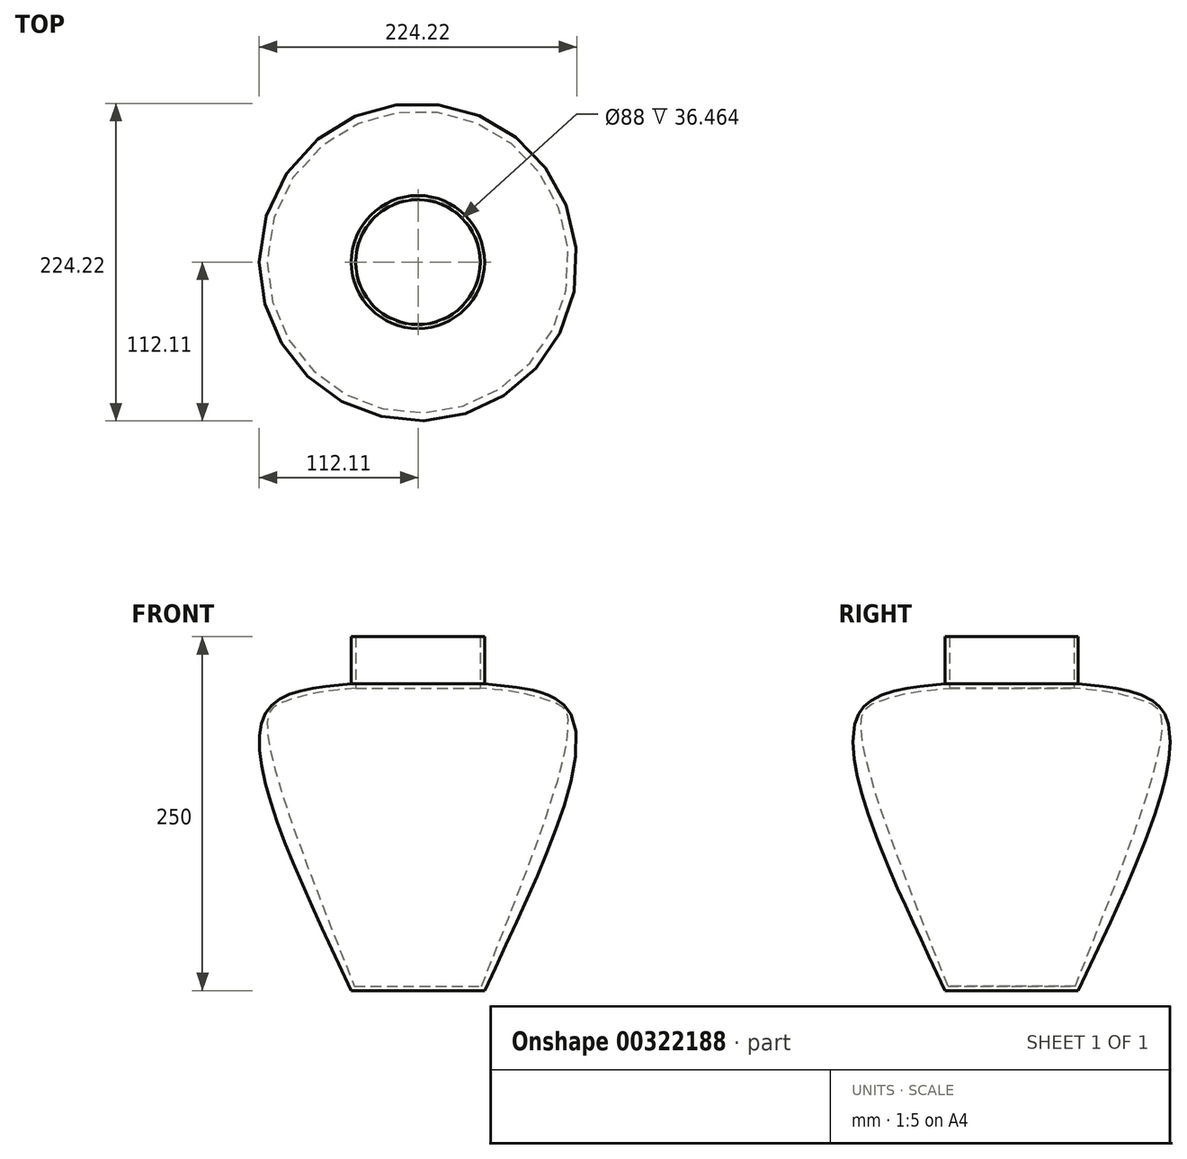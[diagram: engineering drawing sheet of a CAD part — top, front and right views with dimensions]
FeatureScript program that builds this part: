
annotation { "Feature Type Name" : "Feature", "Feature Type Description" : "" }
export const myFeature = defineFeature(function(context is Context, id is Id, definition is map)
    precondition{}
    {
        {
            var Q0;
            Q0=qCreatedBy(makeId("Right.planeOp"),FACE);
            var sketch = newSketch(context, id + "F0", { "sketchPlane" : qUnion([Q0])});
            skLineSegment(sketch, "E0", {"start": v(-47, 143.2) * mm, "end": v(-47, 109.84) * mm});
            skFitSpline(sketch, "E1", {"points": [v(-47, 109.84) * mm, v(-109.07, 86.56) * mm, v(-47, -106.8) * mm], "startDerivative": vector(-206.76, -21.49) * mm, "endDerivative": vector(151.73, -322.02) * mm});
            skLineSegment(sketch, "E2", {"start": v(-47, -106.8) * mm, "end": v(0, -106.8) * mm});
            skLineSegment(sketch, "E3", {"start": v(-47, 143.2) * mm, "end": v(-44, 143.2) * mm});
            skLineSegment(sketch, "E4", {"start": v(-44, 143.2) * mm, "end": v(-44, 109.9) * mm});
            skLineSegment(sketch, "E5", {"start": v(0, -103.8) * mm, "end": v(0, -106.8) * mm});
            skLineSegment(sketch, "E6", {"start": v(-44, 109.9) * mm, "end": v(-44, 106.74) * mm});
            skFitSpline(sketch, "E7", {"points": [v(-44, 106.74) * mm, v(-71.13, 103.65) * mm, v(-94.78, 97.15) * mm, v(-105.96, 86.56) * mm, v(-44.88, -103.8) * mm], "startDerivative": vector(-147.3, -11.54) * mm, "endDerivative": vector(198.39, -499.08) * mm});
            skLineSegment(sketch, "E8", {"start": v(0, -103.8) * mm, "end": v(-44.88, -103.8) * mm});
            skLineSegment(sketch, "E9", {"start": v(0, -106.8) * mm, "end": v(0, 190.13) * mm});
            skSolve(sketch);
        }
        {
            var Q0;
            Q0=makeQuery(id+"F0.imprint","IMPRINT",FACE,{"disambiguationData":[TD([[makeQuery(id+"F0.imprint","IMPRINT",EDGE,{"derivedFrom":sQuery(id+"F0.wireOp",EDGE,"E0")}),1.0]])]});
            var Q1;
            Q1=sQuery(id+"F0.wireOp",EDGE,"E9");
            revolve(context, id + "F1", {"entities" : qUnion([Q0]), "axis" : qUnion([Q1]), "revolveType" : RevolveType.FULL});
        }
    });
